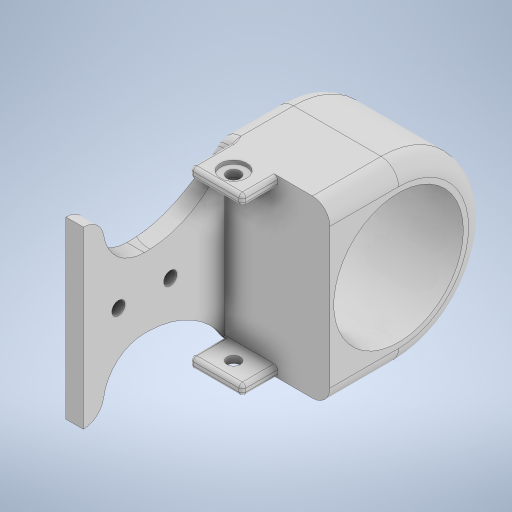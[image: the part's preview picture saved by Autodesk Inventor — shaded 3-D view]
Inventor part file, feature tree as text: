
AUTODESK INVENTOR PART (.ipt)
format: ipt  version: 2024.2 (Build 282272000, 272)  size: 1,206,784 bytes
history: native  units: in
note: dims shown in document units (in); Inventor stores cm internally (conversion verified against a paired STEP export)
features: fillet x7, sketch x6, extrude x6, mirror x2, plane x1
ambient origin geometry x8: Origin, YZ Plane, XZ Plane, XY Plane, X Axis, Y Axis, Z Axis, Center Point
bodies: Solid1 (feature_tree)
feature tree (22):
  sketch  "Sketch1"  dims[d2=0.15in d3=0.5827in]
  extrude  "Extrusion1"  Depth=0.5827in
  extrude  "Extrusion2"  Depth=0.3937in
  extrude  "Extrusion3"  Depth=0.7874in
  fillet  "Fillet1"  Radius=0.7874in
  extrude  "Extrusion6"  Depth=0.1in
  plane  "Work Plane1"
  extrude  "Extrusion7"  Depth=0.6142in
  mirror  "Mirror1"
  fillet  "Fillet2"  Radius=1.4724in
  extrude  "Extrusion8"  Depth=0.1969in TaperAngle=360.0deg
  mirror  "Mirror2"
  fillet  "Fillet3"  Radius=0.315in
  fillet  "Fillet4"  Radius=1.0787in
  fillet  "Fillet5"  Radius=0.1575in
  fillet  "Fillet6"  Radius=0.1575in
  fillet  "Fillet7"  Radius=2.3622in
  sketch  "Sketch2"  dims[d5=0.3937in d6=0.2913in]
  sketch  "Sketch3"  dims[d7=0.3937in d8=0.5906in d9=0.7874in]
  sketch  "Sketch6"  dims[d10=1.4724in d15=0.1in]
  sketch  "Sketch7"  dims[d17=1.0394in d18=0.6142in d19=1.4724in]
  sketch  "Sketch8"  dims[d20=0.4528in d21=2.3622in d23=360.0deg d25=0.315in d26=1.0787in d27=0.1575in d28=0.1575in d29=2.3622in d31=360.0deg d33=0.1969in d34=0.0in d35=0.311in d36=0.311in d37=0.2323in d38=0.2323in d39=0.2323in d40=0.2323in d41=0.2323in d42=0.2323in d43=0.0984in d44=0.0in d45=1.4567in d47=0.7717in d49=1.1811in d50=0.0in d52=0.0591in d58=0.1969in d66=1.0236in d67=0.5906in d68=0.3937in d69=0.1181in d70=0.0in d71=0.15in d72=0.2953in d73=0.0394in d74=0.0in d75=1.9685in d76=0.5906in d77=0.3937in d78=0.0in d79=0.3937in d80=0.1969in d81=0.0394in d82=0.0394in d83=0.0394in d84=0.1969in]
